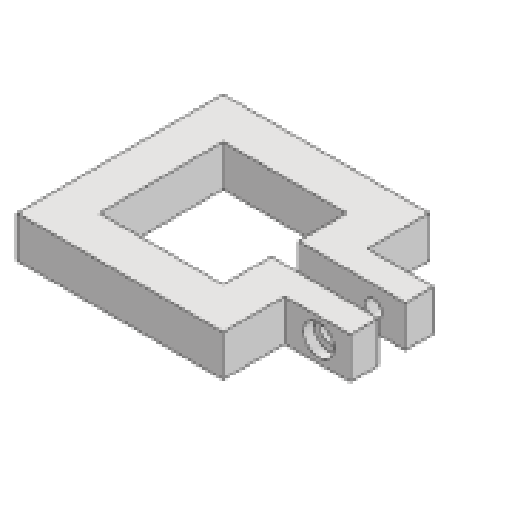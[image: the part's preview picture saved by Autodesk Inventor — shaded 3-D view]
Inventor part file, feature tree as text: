
AUTODESK INVENTOR PART (.ipt)
format: ipt  version: 2025 (Build 290162000, 162)  size: 265,728 bytes
history: native  units: mm
features: extrude x11, sketch x11, projected_geometry x9, other x4, reference x2, fillet x1
ambient origin geometry x8: Origin, YZ Plane, XZ Plane, XY Plane, X Axis, Y Axis, Z Axis, Center Point
bodies: Solid1 (feature_tree)
feature tree (38):
  extrude  "Extrusion1"  Depth=30.0mm
  extrude  "Extrusion2"  Depth=10.0mm
  extrude  "Extrusion3"  Depth=25.0mm
  extrude  "Extrusion4"  Depth=25.0mm
  extrude  "Extrusion5"  TaperAngle=0.0deg  [1 undecoded]
  extrude  "Extrusion6"  Depth=10.0mm TaperAngle=0.0deg
  extrude  "Extrusion7"  Depth=10.0mm
  extrude  "Extrusion8"  TaperAngle=0.0deg  [1 undecoded]
  extrude  "Extrusion9"  Depth=15.0mm TaperAngle=0.0deg
  extrude  "Extrusion10"  Depth=8.2mm TaperAngle=0.0deg
  extrude  "Extrusion11"  Depth=10.0mm
  fillet  "Fillet2"  [1 undecoded]
  sketch  "Sketch1"  dims[d0=30.0mm d1=30.0mm]
  sketch  "Sketch2"  dims[d2=10.0mm d4=44.45mm]
  projected_geometry  "Projected Loop1"
  sketch  "Sketch3"  dims[d5=10.0mm d6=0.0mm d7=25.0mm]
  projected_geometry  "Projected Loop2"
  sketch  "Sketch4"  dims[d8=25.0mm d9=0.0mm d10=20.0mm]
  projected_geometry  "Projected Loop3"
  sketch  "Sketch5"  dims[d11=2.7mm d12=0.0mm d13=0.0mm]
  sketch  "Sketch6"  dims[d15=4.0mm d16=10.0mm d17=0.0mm]
  projected_geometry  "Projected Loop4"
  sketch  "Sketch7"  dims[d18=5.0mm d19=0.0mm d20=10.0mm]
  projected_geometry  "Projected Loop5"
  sketch  "Sketch8"  dims[d21=10.0mm d22=0.0mm d23=0.0mm]
  projected_geometry  "Projected Loop6"
  sketch  "Sketch9"  dims[d24=0.0mm d25=0.0mm d26=15.0mm d27=0.0mm]
  projected_geometry  "Projected Loop7"
  sketch  "Sketch10"  dims[d28=8.2mm d29=15.0mm d30=0.0mm]
  projected_geometry  "Projected Loop8"
  sketch  "Sketch11"  dims[d31=10.0mm d32=0.0mm d33=5.5mm d34=0.0mm d35=0.0mm d36=10.0mm]
  reference  "Reference1"
  reference  "Reference2"
  projected_geometry  "Projected Loop9"
  other  "<userpath>\Desktop\puppycat\woodhouseMK1.iam"
  other  "woodhouseMK1.iam"
  other  "upperFrontSkidPlate:1"
  other  "horizontalStrut:1"
note: 3 required parameter values undecoded (feature->parameter linkage not recoverable at this tier; creation-order binding heuristic only, values carry confidence <= 0.55)
